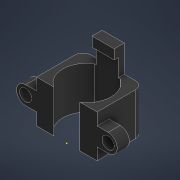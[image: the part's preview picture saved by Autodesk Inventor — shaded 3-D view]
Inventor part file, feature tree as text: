
AUTODESK INVENTOR PART (.ipt)
format: ipt  version: 2021 (Build 250183000, 183)  size: 247,808 bytes
history: native  units: mm
features: other x11, extrude x10, sketch x10, fillet x1
ambient origin geometry x8: Origin, YZ Plane, XZ Plane, XY Plane, X Axis, Y Axis, Z Axis, Center Point
bodies: Body1 (feature_tree)
feature tree (32):
  other  "Suporte Externo - Motor"
  other  "Sólido1"
  extrude  "Extrusão1"  Depth=1.5mm TaperAngle=0.0deg
  extrude  "Extrusão2"  Depth=5.0mm TaperAngle=0.0deg
  sketch  "Esboço3"  dims[d11=0.5mm d12=0.5mm]
  extrude  "Extrusão3"  Depth=0.5mm
  extrude  "Extrusão4"  Depth=1.0mm TaperAngle=0.0deg
  extrude  "Extrusão5"  Depth=3.0mm TaperAngle=0.0deg
  extrude  "Extrusão6"  Depth=0.5mm
  sketch  "Esboço6"  dims[d20=0.5mm d21=0.5mm]
  other  "Plano de trabalho1"
  extrude  "Extrusão7"  Depth=0.5mm
  other  "Plano de trabalho2"
  extrude  "Extrusão8"  TaperAngle=0.0deg  [1 undecoded]
  extrude  "Extrusão9"  Depth=4.5mm
  extrude  "Extrusão10"  TaperAngle=0.0deg  [1 undecoded]
  fillet  "Arredondamento1"  Radius=3.0mm
  sketch  "Esboço1"  dims[d0=15.0mm d1=11.5mm d2=1.5mm d3=11.5mm d4=1.5mm d5=1.5mm d6=13.5mm d7=0.0mm]
  sketch  "Esboço2"  dims[d8=6.5mm d9=5.0mm d10=0.0mm]
  sketch  "Esboço4"  dims[d13=0.5mm d14=1.0mm d15=0.0mm]
  other  "Contorno projetado1"
  other  "Contorno projetado2"
  sketch  "Esboço5"  dims[d16=0.5mm d17=0.0mm d18=3.0mm d19=0.0mm]
  sketch  "Esboço7"  dims[d22=0.5mm d23=0.5mm]
  sketch  "Esboço8"  dims[d24=0.0mm d25=0.0mm d26=0.0mm]
  other  "Contorno projetado3"
  sketch  "Esboço9"  dims[d28=3.0mm d29=4.5mm]
  other  "Contorno projetado4"
  other  "Contorno projetado5"
  sketch  "Esboço10"  dims[d30=3.0mm d31=0.0mm d32=0.0mm d33=3.0mm d34=0.0mm d35=10.0mm d36=0.0mm d37=0.0mm d38=0.0mm d39=2.0mm]
  other  "Contorno projetado6"
  other  "Contorno projetado7"
note: 2 required parameter values undecoded (feature->parameter linkage not recoverable at this tier; creation-order binding heuristic only, values carry confidence <= 0.55)
